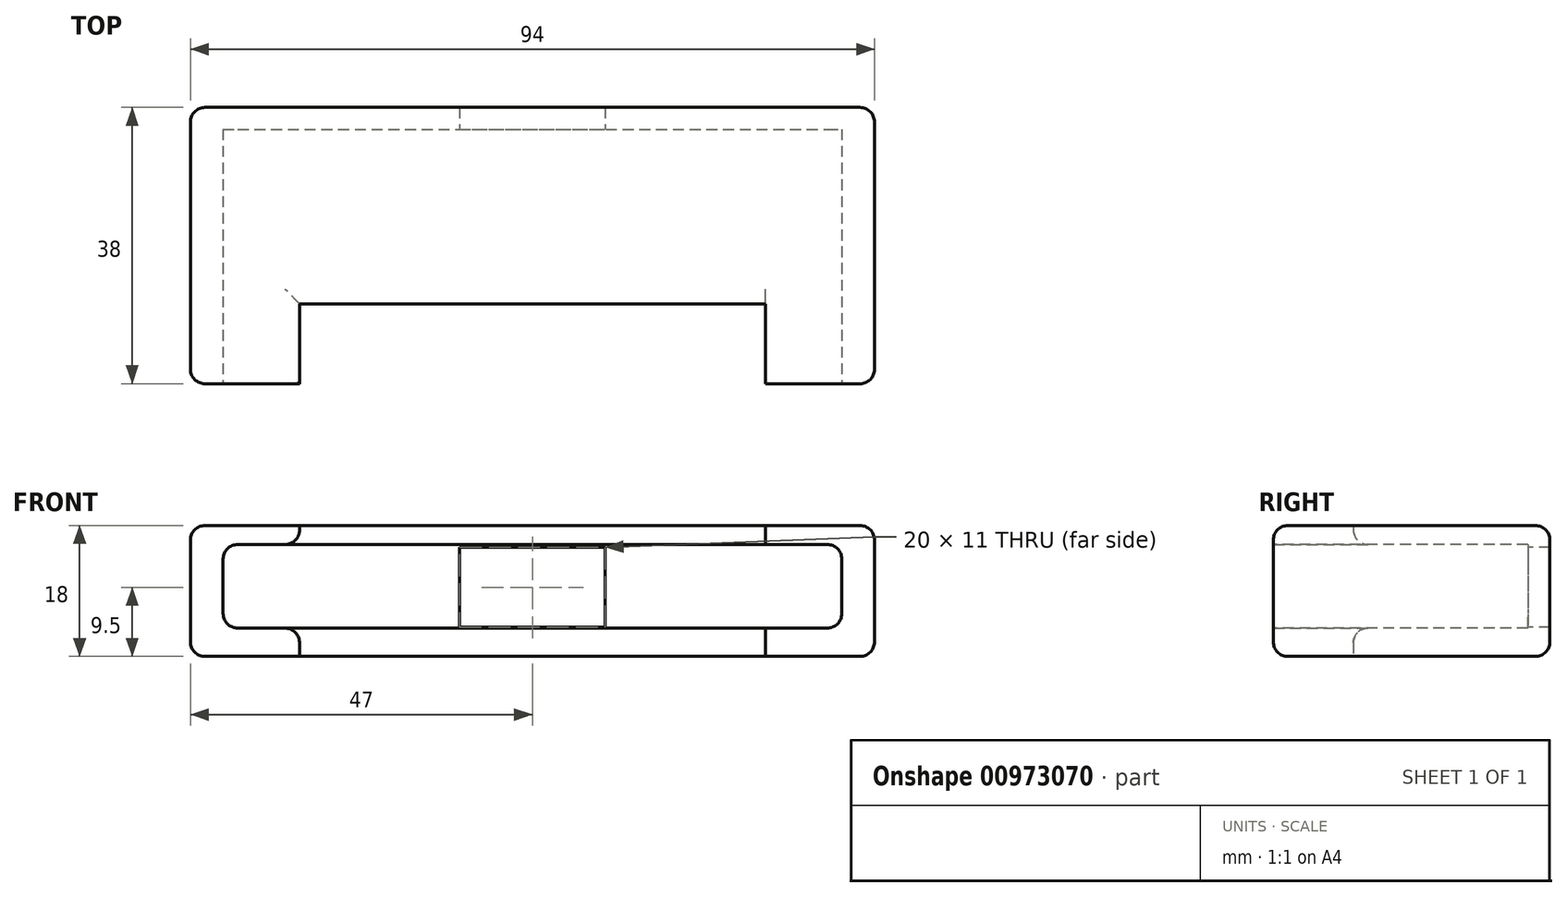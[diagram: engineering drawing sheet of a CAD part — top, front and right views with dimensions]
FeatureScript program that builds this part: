
annotation { "Feature Type Name" : "Feature", "Feature Type Description" : "" }
export const myFeature = defineFeature(function(context is Context, id is Id, definition is map)
    precondition{}
    {
        {
            var Q0;
            Q0=qCreatedBy(makeId("Top.planeOp"),FACE);
            var sketch = newSketch(context, id + "F0", { "sketchPlane" : qUnion([Q0])});
            skLineSegment(sketch, "E0", {"start": v(0, 35) * mm, "end": v(-42.5, 35) * mm});
            skLineSegment(sketch, "E1", {"start": v(-42.5, 35) * mm, "end": v(-42.5, 0) * mm});
            skLineSegment(sketch, "E2", {"start": v(-42.5, 0) * mm, "end": v(0, 0) * mm});
            skLineSegment(sketch, "E3.MirrorCS", {"start": v(0, 35) * mm, "end": v(42.5, 35) * mm});
            skLineSegment(sketch, "E4.MirrorCS", {"start": v(42.5, 35) * mm, "end": v(42.5, 0) * mm});
            skLineSegment(sketch, "E5.MirrorCS", {"start": v(42.5, 0) * mm, "end": v(0, 0) * mm});
            skSolve(sketch);
        }
        {
            var Q0;
            Q0=qCreatedBy(makeId("Top.planeOp"),FACE);
            var sketch = newSketch(context, id + "F1", { "sketchPlane" : qUnion([Q0])});
            skLineSegment(sketch, "E6", {"start": v(-47, 38) * mm, "end": v(-47, 0) * mm});
            skLineSegment(sketch, "E7", {"start": v(-47, 0) * mm, "end": v(-32, 0) * mm});
            skLineSegment(sketch, "E8", {"start": v(-32, 0) * mm, "end": v(-32, 11) * mm});
            skLineSegment(sketch, "E9", {"start": v(-32, 11) * mm, "end": v(0, 11) * mm});
            skLineSegment(sketch, "E10", {"start": v(-47, 38) * mm, "end": v(0, 38) * mm});
            skLineSegment(sketch, "E11.MirrorCS", {"start": v(47, 38) * mm, "end": v(47, 0) * mm});
            skLineSegment(sketch, "E12.MirrorCS", {"start": v(47, 0) * mm, "end": v(32, 0) * mm});
            skLineSegment(sketch, "E13.MirrorCS", {"start": v(32, 0) * mm, "end": v(32, 11) * mm});
            skLineSegment(sketch, "E14.MirrorCS", {"start": v(47, 38) * mm, "end": v(0, 38) * mm});
            skLineSegment(sketch, "E15.MirrorCS", {"start": v(32, 11) * mm, "end": v(0, 11) * mm});
            skSolve(sketch);
        }
        {
            var Q0;
            Q0=qSketchRegion(id+"F1",true);
            extrude(context, id + "F2", {"entities" : qUnion([Q0]), "depth" : 18 * mm, "offsetDistance" : 25 * mm});
        }
        {
            var Q0;
            Q0=qSketchRegion(id+"F0",true);
            extrude(context, id + "F3", {"entities" : qUnion([Q0]), "operationType" : NewBodyOperationType.REMOVE, "depth" : 15.4 * mm, "offsetDistance" : 25 * mm, "hasSecondDirection" : true, "secondDirectionOppositeDirection" : false, "secondDirectionDepth" : 3.9 * mm});
        }
        {
            var Q0;
            Q0=makeQuery(id+"F2.opExtrude","SWEPT_EDGE",EDGE,{"disambiguationData":[OSD([sQuery(id+"F1.wireOp",EDGE,"E6"),sQuery(id+"F1.wireOp",EDGE,"E10")])]});
            var Q1;
            Q1=makeQuery(id+"F2.opExtrude","SWEPT_EDGE",EDGE,{"disambiguationData":[OSD([sQuery(id+"F1.wireOp",EDGE,"E11.MirrorCS"),sQuery(id+"F1.wireOp",EDGE,"E14.MirrorCS")])]});
            var Q2;
            Q2=makeQuery(id+"F2.opExtrude","SWEPT_EDGE",EDGE,{"disambiguationData":[OSD([sQuery(id+"F1.wireOp",EDGE,"E11.MirrorCS"),sQuery(id+"F1.wireOp",EDGE,"E12.MirrorCS")])]});
            var Q3;
            Q3=makeQuery(id+"F2.opExtrude","SWEPT_EDGE",EDGE,{"disambiguationData":[OSD([sQuery(id+"F1.wireOp",EDGE,"E6"),sQuery(id+"F1.wireOp",EDGE,"E7")])]});
            var Q4;
            {var subQ0=sQuery(id+"F0.wireOp",EDGE,"E5.MirrorCS");var subQ1=sQuery(id+"F0.wireOp",EDGE,"E2");Q4=makeQuery(id+"F3.boolean.opBoolean","COPY",EDGE,{"disambiguationData":[topologyDisambiguationEdgeConnected([makeQuery(id+"F2.opExtrude","SWEPT_FACE",FACE,{"disambiguationData":[OSD([sQuery(id+"F1.wireOp",EDGE,"E7")])]})])],"derivedFrom":makeQuery(id+"F3.opExtrude","CAP_EDGE",EDGE,{"disambiguationData":[OSD([subQ1,subQ0])],"isStart":true})});}
            var Q5;
            Q5=makeQuery(id+"F3.boolean.opBoolean","INTERSECT",EDGE,{"derivedFrom":[makeQuery(id+"F2.opExtrude","SWEPT_FACE",FACE,{"disambiguationData":[OSD([sQuery(id+"F1.wireOp",EDGE,"E8")])]}),makeQuery(id+"F3.opExtrude","CAP_FACE",FACE,{"disambiguationData":[OSD([sQuery(id+"F0.wireOp",EDGE,"E0"),sQuery(id+"F0.wireOp",EDGE,"E1"),sQuery(id+"F0.wireOp",EDGE,"E2"),sQuery(id+"F0.wireOp",EDGE,"E3.MirrorCS"),sQuery(id+"F0.wireOp",EDGE,"E4.MirrorCS"),sQuery(id+"F0.wireOp",EDGE,"E5.MirrorCS")])],"isStart":true})]});
            var Q6;
            {var subQ0=sQuery(id+"F0.wireOp",EDGE,"E5.MirrorCS");var subQ1=sQuery(id+"F0.wireOp",EDGE,"E2");Q6=makeQuery(id+"F3.boolean.opBoolean","COPY",EDGE,{"disambiguationData":[topologyDisambiguationEdgeConnected([makeQuery(id+"F2.opExtrude","SWEPT_FACE",FACE,{"disambiguationData":[OSD([sQuery(id+"F1.wireOp",EDGE,"E7")])]})])],"derivedFrom":makeQuery(id+"F3.opExtrude","CAP_EDGE",EDGE,{"disambiguationData":[OSD([subQ1,subQ0])],"isStart":false})});}
            var Q7;
            Q7=makeQuery(id+"F3.boolean.opBoolean","COPY",EDGE,{"derivedFrom":makeQuery(id+"F3.opExtrude","CAP_EDGE",EDGE,{"disambiguationData":[OSD([sQuery(id+"F0.wireOp",EDGE,"E1")])],"isStart":false})});
            var Q8;
            Q8=makeQuery(id+"F3.boolean.opBoolean","INTERSECT",EDGE,{"derivedFrom":[makeQuery(id+"F2.opExtrude","SWEPT_FACE",FACE,{"disambiguationData":[OSD([sQuery(id+"F1.wireOp",EDGE,"E8")])]}),makeQuery(id+"F3.opExtrude","CAP_FACE",FACE,{"disambiguationData":[OSD([sQuery(id+"F0.wireOp",EDGE,"E0"),sQuery(id+"F0.wireOp",EDGE,"E1"),sQuery(id+"F0.wireOp",EDGE,"E2"),sQuery(id+"F0.wireOp",EDGE,"E3.MirrorCS"),sQuery(id+"F0.wireOp",EDGE,"E4.MirrorCS"),sQuery(id+"F0.wireOp",EDGE,"E5.MirrorCS")])],"isStart":false})]});
            var Q9;
            Q9=makeQuery(id+"F3.boolean.opBoolean","INTERSECT",EDGE,{"derivedFrom":[makeQuery(id+"F2.opExtrude","SWEPT_FACE",FACE,{"disambiguationData":[OSD([sQuery(id+"F1.wireOp",EDGE,"E9"),sQuery(id+"F1.wireOp",EDGE,"E15.MirrorCS")])]}),makeQuery(id+"F3.opExtrude","CAP_FACE",FACE,{"disambiguationData":[OSD([sQuery(id+"F0.wireOp",EDGE,"E0"),sQuery(id+"F0.wireOp",EDGE,"E1"),sQuery(id+"F0.wireOp",EDGE,"E2"),sQuery(id+"F0.wireOp",EDGE,"E3.MirrorCS"),sQuery(id+"F0.wireOp",EDGE,"E4.MirrorCS"),sQuery(id+"F0.wireOp",EDGE,"E5.MirrorCS")])],"isStart":false})]});
            var Q10;
            {var subQ0=sQuery(id+"F0.wireOp",EDGE,"E5.MirrorCS");var subQ1=sQuery(id+"F0.wireOp",EDGE,"E2");Q10=makeQuery(id+"F3.boolean.opBoolean","COPY",EDGE,{"disambiguationData":[topologyDisambiguationEdgeConnected([makeQuery(id+"F2.opExtrude","SWEPT_FACE",FACE,{"disambiguationData":[OSD([sQuery(id+"F1.wireOp",EDGE,"E12.MirrorCS")])]})])],"derivedFrom":makeQuery(id+"F3.opExtrude","CAP_EDGE",EDGE,{"disambiguationData":[OSD([subQ1,subQ0])],"isStart":false})});}
            var Q11;
            Q11=makeQuery(id+"F3.boolean.opBoolean","COPY",EDGE,{"derivedFrom":makeQuery(id+"F3.opExtrude","SWEPT_EDGE",EDGE,{"disambiguationData":[OSD([sQuery(id+"F0.wireOp",EDGE,"E4.MirrorCS"),sQuery(id+"F0.wireOp",EDGE,"E5.MirrorCS")])]})});
            var Q12;
            {var subQ0=sQuery(id+"F0.wireOp",EDGE,"E5.MirrorCS");var subQ1=sQuery(id+"F0.wireOp",EDGE,"E2");Q12=makeQuery(id+"F3.boolean.opBoolean","COPY",EDGE,{"disambiguationData":[topologyDisambiguationEdgeConnected([makeQuery(id+"F2.opExtrude","SWEPT_FACE",FACE,{"disambiguationData":[OSD([sQuery(id+"F1.wireOp",EDGE,"E12.MirrorCS")])]})])],"derivedFrom":makeQuery(id+"F3.opExtrude","CAP_EDGE",EDGE,{"disambiguationData":[OSD([subQ1,subQ0])],"isStart":true})});}
            var Q13;
            Q13=makeQuery(id+"F3.boolean.opBoolean","INTERSECT",EDGE,{"derivedFrom":[makeQuery(id+"F2.opExtrude","SWEPT_FACE",FACE,{"disambiguationData":[OSD([sQuery(id+"F1.wireOp",EDGE,"E9"),sQuery(id+"F1.wireOp",EDGE,"E15.MirrorCS")])]}),makeQuery(id+"F3.opExtrude","CAP_FACE",FACE,{"disambiguationData":[OSD([sQuery(id+"F0.wireOp",EDGE,"E0"),sQuery(id+"F0.wireOp",EDGE,"E1"),sQuery(id+"F0.wireOp",EDGE,"E2"),sQuery(id+"F0.wireOp",EDGE,"E3.MirrorCS"),sQuery(id+"F0.wireOp",EDGE,"E4.MirrorCS"),sQuery(id+"F0.wireOp",EDGE,"E5.MirrorCS")])],"isStart":true})]});
            fillet(context, id + "F4", {"entities" : qUnion([Q0, Q1, Q2, Q3, Q4, Q5, Q6, Q7, Q8, Q9, Q10, Q11, Q12, Q13]), "radius" : 2 * mm, "tangentPropagation" : true, "allowEdgeOverflow" : false});
        }
        {
            var Q0;
            Q0=makeQuery(id+"F2.opExtrude","CAP_EDGE",EDGE,{"disambiguationData":[OSD([sQuery(id+"F1.wireOp",EDGE,"E6")])],"isStart":true});
            var Q1;
            Q1=makeQuery(id+"F2.opExtrude","CAP_EDGE",EDGE,{"disambiguationData":[OSD([sQuery(id+"F1.wireOp",EDGE,"E6")])],"isStart":false});
            fillet(context, id + "F5", {"entities" : qUnion([Q0, Q1]), "radius" : 2 * mm, "tangentPropagation" : true, "allowEdgeOverflow" : false});
        }
        {
            var Q0;
            Q0=qCreatedBy(makeId("Top.planeOp"),FACE);
            var sketch = newSketch(context, id + "F6", { "sketchPlane" : qUnion([Q0])});
            skLineSegment(sketch, "E16.bottom", {"start": v(-10, 39.89) * mm, "end": v(10, 39.89) * mm});
            skLineSegment(sketch, "E16.top", {"start": v(-10, 32.7) * mm, "end": v(10, 32.7) * mm});
            skLineSegment(sketch, "E16.left", {"start": v(-10, 39.89) * mm, "end": v(-10, 32.7) * mm});
            skLineSegment(sketch, "E16.right", {"start": v(10, 39.89) * mm, "end": v(10, 32.7) * mm});
            skPoint(sketch, "E16.middle", {"position": v(0, 36.3) * mm});
            skSolve(sketch);
        }
        {
            var Q0;
            Q0 = qSketchRegion(id + "F6", true);
            extrude(context, id + "F7", {"entities" : qUnion([Q0]), "operationType" : NewBodyOperationType.REMOVE, "depth" : 15 * mm, "offsetDistance" : 25 * mm, "hasSecondDirection" : true, "secondDirectionOppositeDirection" : false, "secondDirectionDepth" : 4 * mm});
        }
        {
            var Q0;
            Q0=makeQuery(id+"F3.boolean.opBoolean","COPY",EDGE,{"derivedFrom":makeQuery(id+"F3.opExtrude","CAP_EDGE",EDGE,{"disambiguationData":[OSD([sQuery(id+"F0.wireOp",EDGE,"E1")])],"isStart":true})});
            var Q1;
            Q1=makeQuery(id+"F3.boolean.opBoolean","COPY",EDGE,{"derivedFrom":makeQuery(id+"F3.opExtrude","CAP_EDGE",EDGE,{"disambiguationData":[OSD([sQuery(id+"F0.wireOp",EDGE,"E4.MirrorCS")])],"isStart":true})});
            var Q2;
            Q2=makeQuery(id+"F3.boolean.opBoolean","COPY",EDGE,{"derivedFrom":makeQuery(id+"F3.opExtrude","CAP_EDGE",EDGE,{"disambiguationData":[OSD([sQuery(id+"F0.wireOp",EDGE,"E4.MirrorCS")])],"isStart":false})});
            fillet(context, id + "F8", {"entities" : qUnion([Q0, Q1, Q2]), "radius" : 2 * mm, "tangentPropagation" : true, "allowEdgeOverflow" : false});
        }
    });
